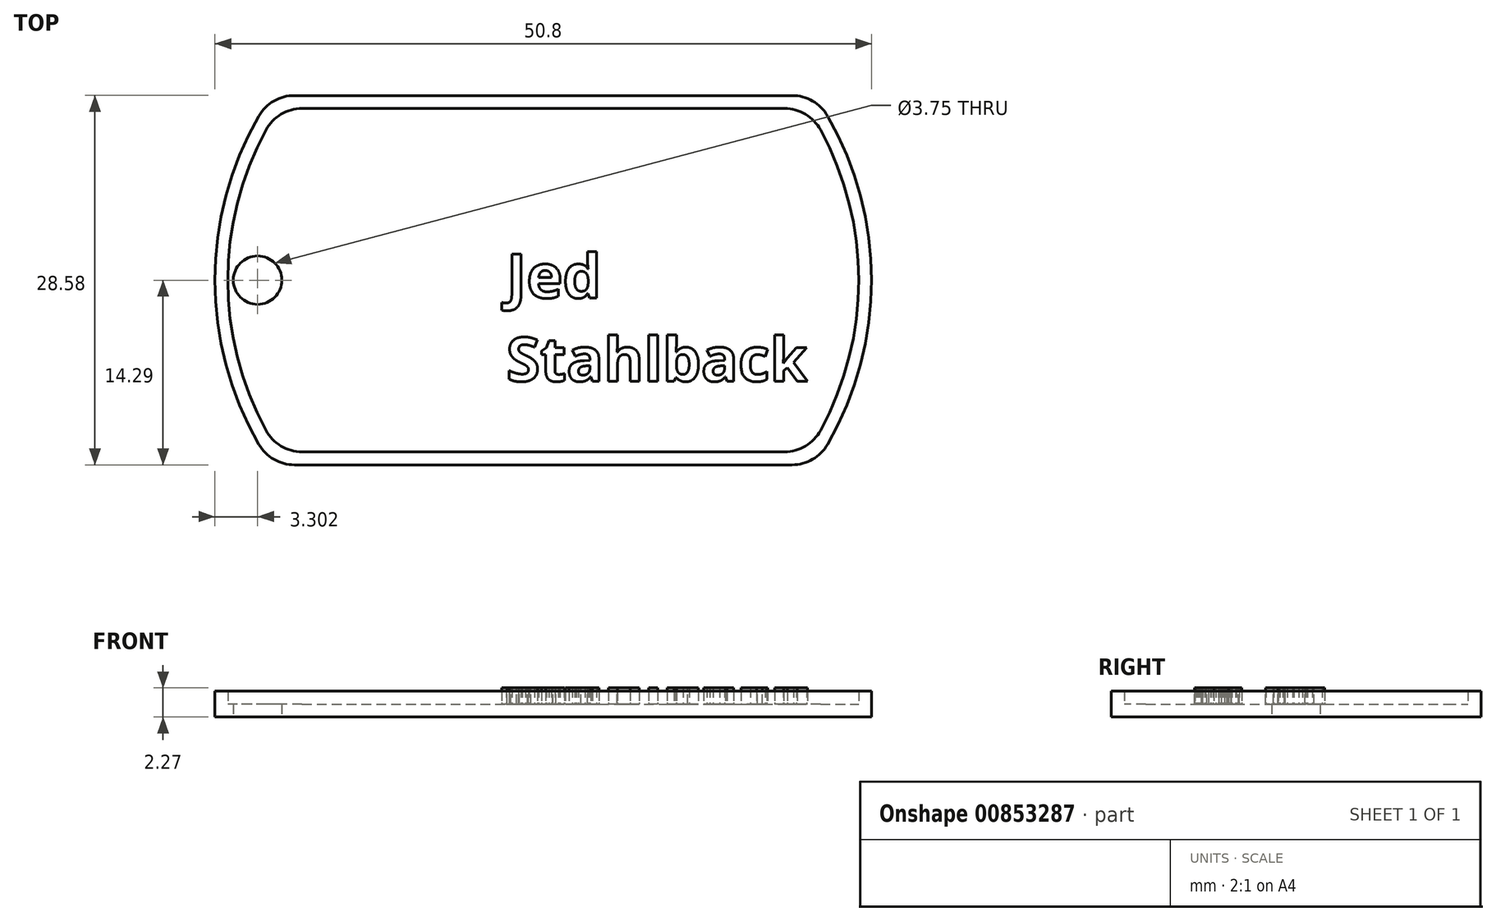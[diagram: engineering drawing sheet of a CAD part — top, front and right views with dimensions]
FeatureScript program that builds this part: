
annotation { "Feature Type Name" : "Feature", "Feature Type Description" : "" }
export const myFeature = defineFeature(function(context is Context, id is Id, definition is map)
    precondition{}
    {
        {
            var Q0;
            Q0=qCreatedBy(makeId("Top.planeOp"),FACE);
            var sketch = newSketch(context, id + "F0", { "sketchPlane" : qUnion([Q0])});
            skArc(sketch, "E0", {"start": v(-22, 12.7) * mm, "mid": v(-25.4, 0) * mm, "end": v(-22, -12.7) * mm});
            skLineSegment(sketch, "E1.top", {"start": v(-19.25, -14.29) * mm, "end": v(19.25, -14.29) * mm});
            skArc(sketch, "E2.trimOffspring", {"start": v(22, -12.7) * mm, "mid": v(25.4, 0) * mm, "end": v(22, 12.7) * mm});
            skLineSegment(sketch, "E3", {"start": v(-19.25, 14.29) * mm, "end": v(19.25, 14.29) * mm});
            skPoint(sketch, "E4.visualSharp", {"position": v(-21, 14.29) * mm});
            skArc(sketch, "E4.filletArc", {"start": v(-19.25, 14.29) * mm, "mid": v(-20.83, 13.86) * mm, "end": v(-22, 12.7) * mm});
            skPoint(sketch, "E5.visualSharp", {"position": v(21, 14.29) * mm});
            skArc(sketch, "E5.filletArc", {"start": v(22, 12.7) * mm, "mid": v(20.83, 13.86) * mm, "end": v(19.25, 14.29) * mm});
            skPoint(sketch, "E6.visualSharp", {"position": v(21, -14.29) * mm});
            skArc(sketch, "E6.filletArc", {"start": v(19.25, -14.29) * mm, "mid": v(20.83, -13.86) * mm, "end": v(22, -12.7) * mm});
            skPoint(sketch, "E7.visualSharp", {"position": v(-21, -14.29) * mm});
            skArc(sketch, "E7.filletArc", {"start": v(-22, -12.7) * mm, "mid": v(-20.83, -13.86) * mm, "end": v(-19.25, -14.29) * mm});
            skCircle(sketch, "E8", {"center": v(-22.1, 0) * mm, "radius": 1.87 * mm});
            skSolve(sketch);
        }
        {
            var Q0;
            Q0=makeQuery(id+"F0.imprint","IMPRINT",FACE,{"disambiguationData":[TD([[makeQuery(id+"F0.imprint","IMPRINT",EDGE,{"derivedFrom":sQuery(id+"F0.wireOp",EDGE,"E0")}),1.0]])]});
            extrude(context, id + "F1", {"entities" : qUnion([Q0]), "depth" : 1 * mm, "offsetDistance" : 25.4 * mm});
        }
        {
            var Q0;
            Q0=makeQuery(id+"F1.opExtrude","CAP_FACE",FACE,{"disambiguationData":[OSD([sQuery(id+"F0.wireOp",EDGE,"E0"),sQuery(id+"F0.wireOp",EDGE,"E1.top"),sQuery(id+"F0.wireOp",EDGE,"E2.trimOffspring"),sQuery(id+"F0.wireOp",EDGE,"E3"),sQuery(id+"F0.wireOp",EDGE,"E4.filletArc"),sQuery(id+"F0.wireOp",EDGE,"E5.filletArc"),sQuery(id+"F0.wireOp",EDGE,"E6.filletArc"),sQuery(id+"F0.wireOp",EDGE,"E7.filletArc")])],"isStart":false});
            var sketch = newSketch(context, id + "F2", { "sketchPlane" : qUnion([Q0])});
            skLineSegment(sketch, "E9.0", {"start": v(-18.66, 13.29) * mm, "end": v(18.66, 13.29) * mm});
            skArc(sketch, "E9.1", {"start": v(-21.45, 11.63) * mm, "mid": v(-24.4, 0) * mm, "end": v(-21.45, -11.63) * mm});
            skLineSegment(sketch, "E9.2", {"start": v(-18.66, -13.29) * mm, "end": v(18.66, -13.29) * mm});
            skArc(sketch, "E9.3", {"start": v(21.45, -11.63) * mm, "mid": v(24.4, 0) * mm, "end": v(21.45, 11.63) * mm});
            skPoint(sketch, "E10.visualSharp", {"position": v(-20.46, 13.29) * mm});
            skArc(sketch, "E10.filletArc", {"start": v(-18.66, 13.29) * mm, "mid": v(-20.29, 12.84) * mm, "end": v(-21.45, 11.63) * mm});
            skPoint(sketch, "E11.visualSharp", {"position": v(20.46, 13.29) * mm});
            skArc(sketch, "E11.filletArc", {"start": v(21.45, 11.63) * mm, "mid": v(20.29, 12.84) * mm, "end": v(18.66, 13.29) * mm});
            skPoint(sketch, "E12.visualSharp", {"position": v(20.46, -13.29) * mm});
            skArc(sketch, "E12.filletArc", {"start": v(18.66, -13.29) * mm, "mid": v(20.29, -12.84) * mm, "end": v(21.45, -11.63) * mm});
            skPoint(sketch, "E13.visualSharp", {"position": v(-20.46, -13.29) * mm});
            skArc(sketch, "E13.filletArc", {"start": v(-21.45, -11.63) * mm, "mid": v(-20.29, -12.84) * mm, "end": v(-18.66, -13.29) * mm});
            skLineSegment(sketch, "E14.0", {"start": v(-19.25, 14.29) * mm, "end": v(19.25, 14.29) * mm});
            skArc(sketch, "E14.1", {"start": v(-22, 12.7) * mm, "mid": v(-25.4, 0) * mm, "end": v(-22, -12.7) * mm});
            skLineSegment(sketch, "E14.2", {"start": v(-19.25, -14.29) * mm, "end": v(19.25, -14.29) * mm});
            skArc(sketch, "E14.3", {"start": v(22, -12.7) * mm, "mid": v(25.4, 0) * mm, "end": v(22, 12.7) * mm});
            skPoint(sketch, "E15.visualSharp", {"position": v(-21, -14.29) * mm});
            skArc(sketch, "E15.filletArc", {"start": v(-22, -12.7) * mm, "mid": v(-20.83, -13.86) * mm, "end": v(-19.25, -14.29) * mm});
            skPoint(sketch, "E16.visualSharp", {"position": v(21, -14.29) * mm});
            skArc(sketch, "E16.filletArc", {"start": v(19.25, -14.29) * mm, "mid": v(20.83, -13.86) * mm, "end": v(22, -12.7) * mm});
            skPoint(sketch, "E17.visualSharp", {"position": v(21, 14.29) * mm});
            skArc(sketch, "E17.filletArc", {"start": v(22, 12.7) * mm, "mid": v(20.83, 13.86) * mm, "end": v(19.25, 14.29) * mm});
            skPoint(sketch, "E18.visualSharp", {"position": v(-21, 14.29) * mm});
            skArc(sketch, "E18.filletArc", {"start": v(-19.25, 14.29) * mm, "mid": v(-20.83, 13.86) * mm, "end": v(-22, 12.7) * mm});
            skSolve(sketch);
        }
        {
            var Q0;
            Q0=makeQuery(id+"F2.imprint","IMPRINT",FACE,{"disambiguationData":[TD([[makeQuery(id+"F2.imprint","IMPRINT",EDGE,{"derivedFrom":sQuery(id+"F2.wireOp",EDGE,"E9.0")}),1.0]])]});
            extrude(context, id + "F3", {"entities" : qUnion([Q0]), "operationType" : NewBodyOperationType.ADD, "depth" : 1 * mm, "offsetDistance" : 25.4 * mm});
        }
        {
            var Q0;
            Q0=makeQuery(id+"F1.opExtrude","CAP_FACE",FACE,{"disambiguationData":[OSD([sQuery(id+"F0.wireOp",EDGE,"E0"),sQuery(id+"F0.wireOp",EDGE,"E1.top"),sQuery(id+"F0.wireOp",EDGE,"E2.trimOffspring"),sQuery(id+"F0.wireOp",EDGE,"E3"),sQuery(id+"F0.wireOp",EDGE,"E4.filletArc"),sQuery(id+"F0.wireOp",EDGE,"E5.filletArc"),sQuery(id+"F0.wireOp",EDGE,"E6.filletArc"),sQuery(id+"F0.wireOp",EDGE,"E7.filletArc"),sQuery(id+"F0.wireOp",EDGE,"E8")])],"isStart":false});
            var sketch = newSketch(context, id + "F4", { "sketchPlane" : qUnion([Q0])});
            skText(sketch, "E19", { "text": "Jed\nStahlback", "fontName": "OpenSans-Bold.ttf"});
            const initialGuessF4  = {"E19": [-0.00286, -0.00138, 1, 0, 0.00341]};
            skSetInitialGuess(sketch, initialGuessF4);
            skSolve(sketch);
        }
        {
            var Q0;
            Q0=qSketchRegion(id+"F4",true);
            extrude(context, id + "F5", {"entities" : qUnion([Q0]), "operationType" : NewBodyOperationType.ADD, "depth" : 1.27 * mm, "offsetDistance" : 25.4 * mm});
        }
    });
